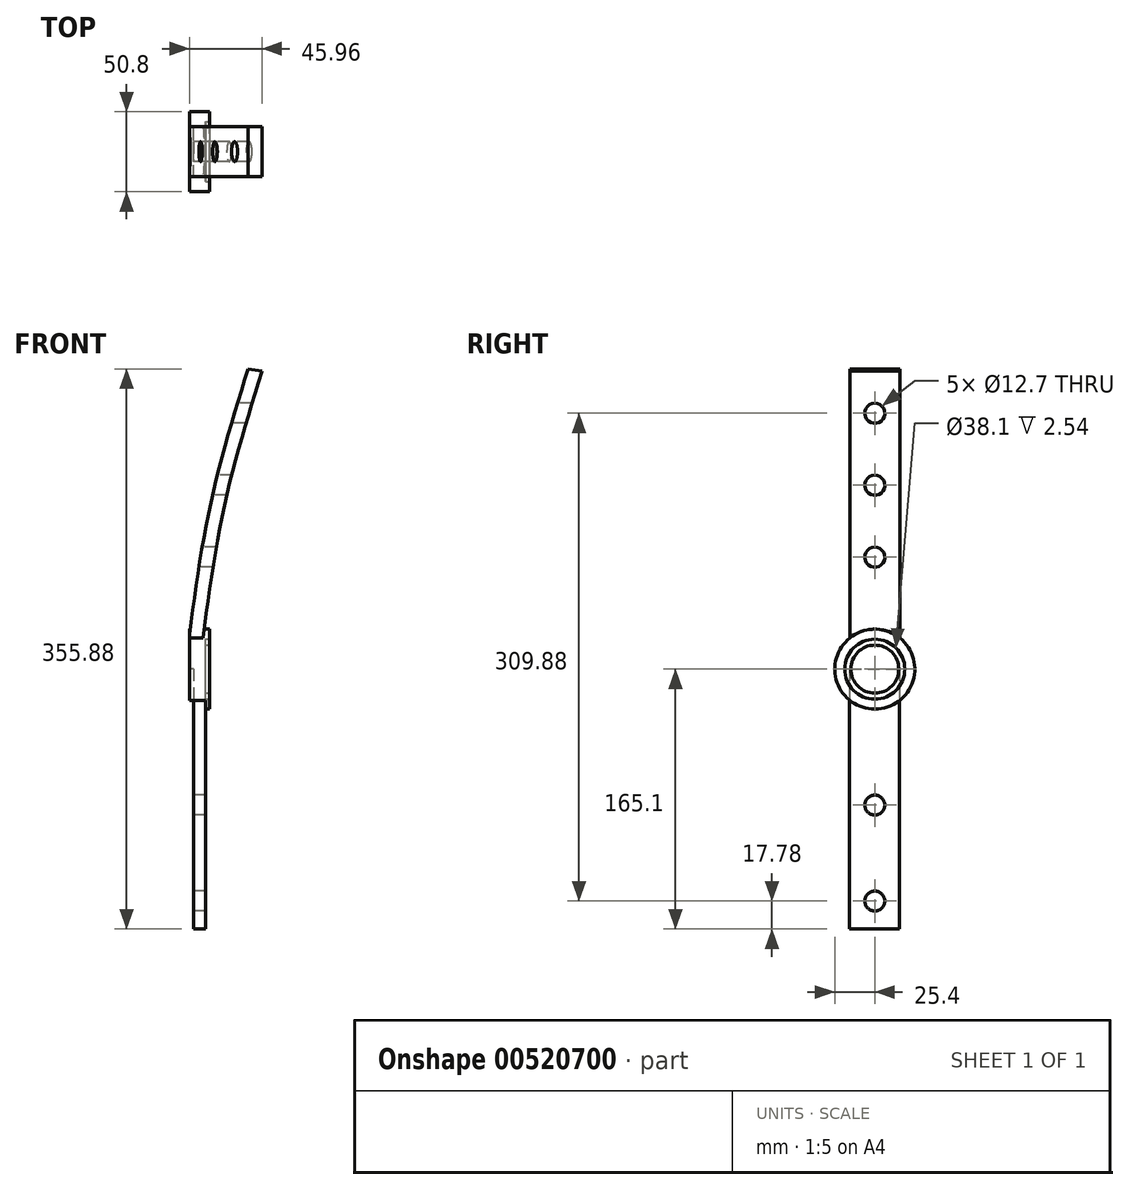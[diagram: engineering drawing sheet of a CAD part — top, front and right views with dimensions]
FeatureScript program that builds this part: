
annotation { "Feature Type Name" : "Feature", "Feature Type Description" : "" }
export const myFeature = defineFeature(function(context is Context, id is Id, definition is map)
    precondition{}
    {
        {
            var Q0;
            Q0=qCreatedBy(makeId("Right.planeOp"),FACE);
            var sketch = newSketch(context, id + "F0", { "sketchPlane" : qUnion([Q0])});
            skCircle(sketch, "E0", {"center": v(0, 0) * mm, "radius": 25.4 * mm});
            skSolve(sketch);
        }
        {
            var Q0;
            Q0=qSketchRegion(id+"F0",true);
            extrude(context, id + "F1", {"entities" : qUnion([Q0]), "depth" : 12.7 * mm, "offsetDistance" : 25.4 * mm});
        }
        {
            var Q0;
            Q0=qCreatedBy(makeId("Right.planeOp"),FACE);
            var sketch = newSketch(context, id + "F2", { "sketchPlane" : qUnion([Q0])});
            skLineSegment(sketch, "E1", {"start": v(-0.09, 0) * mm, "end": v(-15.96, 0) * mm, "construction": true});
            skLineSegment(sketch, "E2", {"start": v(-15.96, 0) * mm, "end": v(0, 0) * mm, "construction": true});
            skLineSegment(sketch, "E3", {"start": v(0, 0) * mm, "end": v(15.88, 0) * mm, "construction": true});
            skLineSegment(sketch, "E4.bottom", {"start": v(-15.96, 0) * mm, "end": v(15.79, 0) * mm});
            skLineSegment(sketch, "E4.top", {"start": v(-15.96, -165.1) * mm, "end": v(15.79, -165.1) * mm});
            skLineSegment(sketch, "E4.left", {"start": v(-15.96, 0) * mm, "end": v(-15.96, -165.1) * mm});
            skLineSegment(sketch, "E4.right", {"start": v(15.79, 0) * mm, "end": v(15.79, -165.1) * mm});
            skSolve(sketch);
        }
        {
            var Q0;
            Q0=makeQuery(id+"F1.opExtrude","CAP_FACE",FACE,{"disambiguationData":[OSD([sQuery(id+"F0.wireOp",EDGE,"E0")])],"isStart":false});
            var sketch = newSketch(context, id + "F3", { "sketchPlane" : qUnion([Q0])});
            skCircle(sketch, "E5", {"center": v(0, 0) * mm, "radius": 19.05 * mm});
            skCircle(sketch, "E6", {"center": v(0, 0) * mm, "radius": 15.24 * mm});
            skSolve(sketch);
        }
        {
            var Q0;
            Q0=qSketchRegion(id+"F2",true);
            extrude(context, id + "F4", {"entities" : qUnion([Q0]), "operationType" : NewBodyOperationType.ADD, "depth" : 10.16 * mm, "offsetDistance" : 25.4 * mm});
        }
        {
            var Q0;
            Q0=qSketchRegion(id+"F3",true);
            extrude(context, id + "F5", {"entities" : qUnion([Q0]), "operationType" : NewBodyOperationType.REMOVE, "oppositeDirection" : true, "depth" : 2.54 * mm, "offsetDistance" : 25.4 * mm});
        }
        {
            var Q0;
            Q0=qSketchRegion(id+"F2",true);
            extrude(context, id + "F6", {"entities" : qUnion([Q0]), "operationType" : NewBodyOperationType.REMOVE, "depth" : 2.54 * mm, "offsetDistance" : 25.4 * mm});
        }
        {
            var Q0;
            Q0=qCreatedBy(makeId("Right.planeOp"),FACE);
            var sketch = newSketch(context, id + "F7", { "sketchPlane" : qUnion([Q0])});
            skLineSegment(sketch, "E7", {"start": v(0, 0) * mm, "end": v(0, 25.4) * mm, "construction": true});
            skLineSegment(sketch, "E8", {"start": v(0, 25.4) * mm, "end": v(0, 71.12) * mm, "construction": true});
            skLineSegment(sketch, "E9", {"start": v(0, 71.12) * mm, "end": v(0, 116.84) * mm, "construction": true});
            skLineSegment(sketch, "E10", {"start": v(0, 116.84) * mm, "end": v(0, 162.56) * mm, "construction": true});
            skLineSegment(sketch, "E11", {"start": v(0, 0) * mm, "end": v(0, -25.4) * mm, "construction": true});
            skLineSegment(sketch, "E12", {"start": v(0, -25.4) * mm, "end": v(0, -86.36) * mm, "construction": true});
            skLineSegment(sketch, "E13", {"start": v(0, -86.36) * mm, "end": v(0, -147.32) * mm, "construction": true});
            skCircle(sketch, "E14", {"center": v(0, 162.56) * mm, "radius": 6.35 * mm});
            skCircle(sketch, "E15", {"center": v(0, 116.84) * mm, "radius": 6.35 * mm});
            skCircle(sketch, "E16", {"center": v(0, 71.12) * mm, "radius": 6.35 * mm});
            skCircle(sketch, "E17", {"center": v(0, -86.36) * mm, "radius": 6.35 * mm});
            skCircle(sketch, "E18", {"center": v(0, -147.32) * mm, "radius": 6.35 * mm});
            skSolve(sketch);
        }
        {
            var Q0;
            Q0=qCreatedBy(makeId("Front.planeOp"),FACE);
            var sketch = newSketch(context, id + "F8", { "sketchPlane" : qUnion([Q0])});
            skFitSpline(sketch, "E19", {"points": [v(0, 0) * mm, v(15.42, 101.37) * mm, v(39.92, 190.3) * mm], "startDerivative": vector(24.86, 201.32) * mm, "endDerivative": vector(55.24, 179.1) * mm});
            skLineSegment(sketch, "E20", {"start": v(0, 0) * mm, "end": v(12.7, 0) * mm});
            skFitSpline(sketch, "E21.0", {"points": [v(12.6, -1.56) * mm, v(13.64, 6.83) * mm, v(15.7, 23.57) * mm, v(18.47, 44.24) * mm, v(20.9, 60.54) * mm, v(22.86, 72.63) * mm, v(24.98, 84.56) * mm, v(26.9, 94.35) * mm, v(28.56, 102.07) * mm, v(30.29, 109.75) * mm, v(32.59, 119.27) * mm, v(35.53, 130.6) * mm, v(39.67, 145.6) * mm, v(45.16, 164.23) * mm, v(49.75, 179.1) * mm, v(52.05, 186.57) * mm]});
            skLineSegment(sketch, "E22", {"start": v(39.92, 190.3) * mm, "end": v(52.62, 190.3) * mm});
            skLineSegment(sketch, "E23", {"start": v(52.05, 186.57) * mm, "end": v(52.62, 190.3) * mm});
            skSolve(sketch);
        }
        {
            var Q0;
            Q0=qCreatedBy(makeId("Top.planeOp"),FACE);
            cPlane(context, id + "F9", {"entities" : qUnion([Q0]), "cplaneType" : CPlaneType.OFFSET, "offset" : 22.1 * mm, "width" : 152.4 * mm, "height" : 152.4 * mm});
        }
        {
            var Q0;
            Q0=qCreatedBy(id+"F9.planeOp",FACE);
            var sketch = newSketch(context, id + "F10", { "sketchPlane" : qUnion([Q0])});
            skLineSegment(sketch, "E24", {"start": v(0, 0) * mm, "end": v(0, 15.88) * mm});
            skLineSegment(sketch, "E25", {"start": v(0, 0) * mm, "end": v(0, -15.88) * mm});
            skLineSegment(sketch, "E26", {"start": v(0, -15.88) * mm, "end": v(8.9, -15.88) * mm});
            skLineSegment(sketch, "E27", {"start": v(8.9, -15.88) * mm, "end": v(8.9, 15.88) * mm});
            skLineSegment(sketch, "E28", {"start": v(8.9, 15.88) * mm, "end": v(0, 15.88) * mm});
            skSolve(sketch);
        }
        {
            var Q0;
            Q0 = qSketchRegion(id + "F10", true);
            var Q1;
            Q1=sQuery(id+"F8.wireOp",EDGE,"E19");
            sweep(context, id + "F11", {"operationType" : NewBodyOperationType.ADD, "profiles" : qUnion([Q0]), "path" : qUnion([Q1])});
        }
        {
            var Q0;
            Q0=qCreatedBy(makeId("Front.planeOp"),FACE);
            var sketch = newSketch(context, id + "F12", { "sketchPlane" : qUnion([Q0])});
            skPoint(sketch, "E29", {"position": v(-83.73, 76.79) * mm});
            skLineSegment(sketch, "E30.bottom", {"start": v(-83.73, 76.79) * mm, "end": v(0, 76.79) * mm});
            skLineSegment(sketch, "E30.top", {"start": v(-83.73, -31.1) * mm, "end": v(0, -31.1) * mm});
            skLineSegment(sketch, "E30.left", {"start": v(-83.73, 76.79) * mm, "end": v(-83.73, -31.1) * mm});
            skLineSegment(sketch, "E30.right", {"start": v(0, 76.79) * mm, "end": v(0, -31.1) * mm});
            skSolve(sketch);
        }
        {
            var Q0;
            Q0 = qSketchRegion(id + "F12", true);
            extrude(context, id + "F13", {"entities" : qUnion([Q0]), "operationType" : NewBodyOperationType.REMOVE, "endBound" : BoundingType.SYMMETRIC, "oppositeDirection" : true, "depth" : 76.2 * mm, "offsetDistance" : 25.4 * mm});
        }
        {
            var Q0;
            Q0 = qSketchRegion(id + "F7", true);
            extrude(context, id + "F14", {"entities" : qUnion([Q0]), "operationType" : NewBodyOperationType.REMOVE, "depth" : 121.16 * mm, "offsetDistance" : 25.4 * mm});
        }
    });
